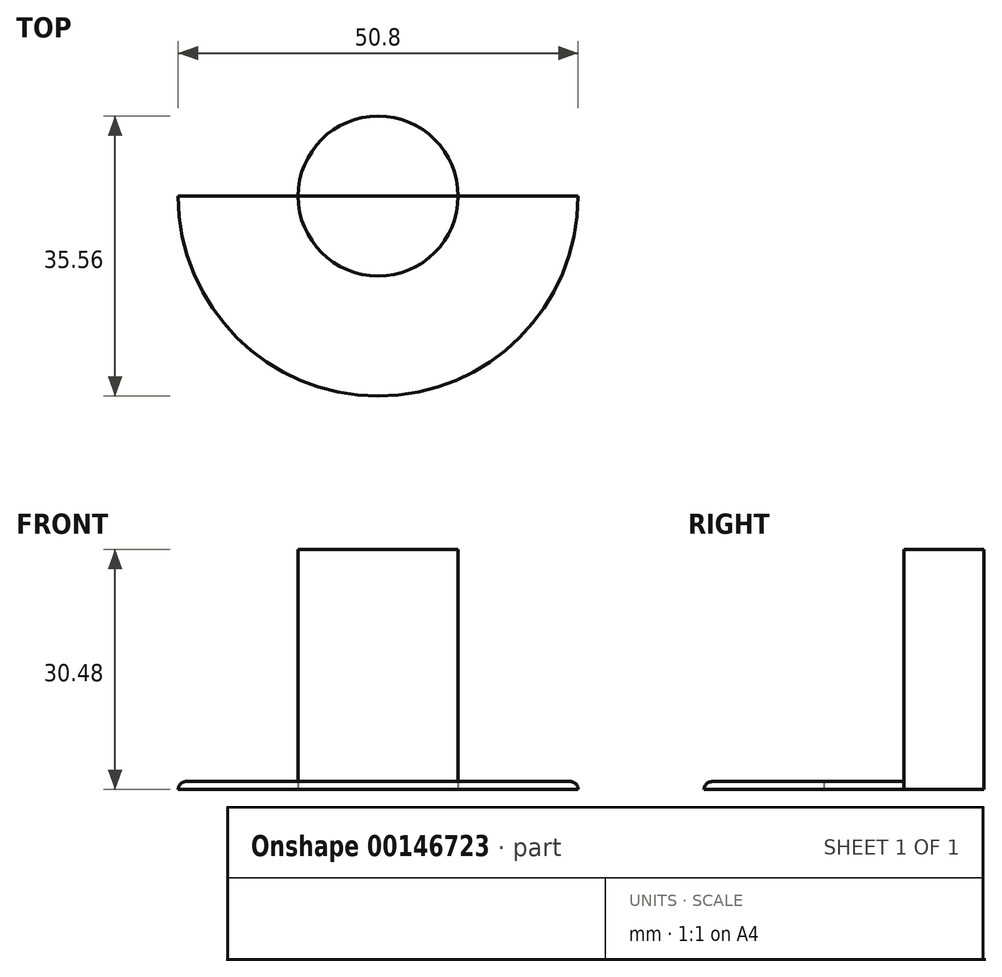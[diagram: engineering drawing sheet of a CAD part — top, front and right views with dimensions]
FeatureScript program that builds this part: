
annotation { "Feature Type Name" : "Feature", "Feature Type Description" : "" }
export const myFeature = defineFeature(function(context is Context, id is Id, definition is map)
    precondition{}
    {
        {
            assignVariable(context, id + "F0", {"name" : "R", "anyValue" : 2});
        }
        {
            var Q0;
            Q0=qCreatedBy(makeId("Top.planeOp"),FACE);
            var sketch = newSketch(context, id + "F1", { "sketchPlane" : qUnion([Q0])});
            skCircle(sketch, "E0", {"center": v(0, 0) * mm, "radius": 25.4 * mm});
            skCircle(sketch, "E1", {"center": v(0, 0) * mm, "radius": 10.16 * mm});
            skLineSegment(sketch, "E2", {"start": v(-25.4, 0) * mm, "end": v(25.4, 0) * mm});
            skSolve(sketch);
        }
        {
            var Q0;
            {var subQ0=sQuery(id+"F1.wireOp",EDGE,"E2");var subQ1=sQuery(id+"F1.wireOp",EDGE,"E0");var subQ2=makeQuery(id+"F1.imprint","INTERSECT",VERTEX,{"disambiguationData":[OD(0.0)],"derivedFrom":[subQ1,subQ0]});Q0=makeQuery(id+"F1.imprint","IMPRINT",FACE,{"disambiguationData":[TD([[makeQuery(id+"F1.imprint","IMPRINT",EDGE,{"disambiguationData":[TD([[subQ2,1.0]])],"derivedFrom":subQ1}),1.0]])]});}
            var Q1;
            {var subQ0=sQuery(id+"F1.wireOp",EDGE,"E2");var subQ1=sQuery(id+"F1.wireOp",EDGE,"E1");var subQ2=makeQuery(id+"F1.imprint","INTERSECT",VERTEX,{"disambiguationData":[OD(0.0)],"derivedFrom":[subQ1,subQ0]});Q1=makeQuery(id+"F1.imprint","IMPRINT",FACE,{"disambiguationData":[TD([[makeQuery(id+"F1.imprint","IMPRINT",EDGE,{"disambiguationData":[TD([[subQ2,1.0]])],"derivedFrom":subQ1}),1.0]])]});}
            extrude(context, id + "F2", {"entities" : qUnion([Q0, Q1]), "depth" : (getVariable(context, 'R') / 2) * mm});
        }
        {
            var Q0;
            Q0=makeQuery(id+"F2.opExtrude","CAP_EDGE",EDGE,{"disambiguationData":[OSD([sQuery(id+"F1.wireOp",EDGE,"E0")])],"isStart":false});
            fillet(context, id + "F3", {"entities" : qUnion([Q0]), "radius" : (getVariable(context, 'R') / 2) * mm, "tangentPropagation" : true, "allowEdgeOverflow" : false});
        }
        {
            var Q0;
            {var subQ0=sQuery(id+"F1.wireOp",EDGE,"E2");var subQ1=sQuery(id+"F1.wireOp",EDGE,"E1");var subQ2=makeQuery(id+"F1.imprint","INTERSECT",VERTEX,{"disambiguationData":[OD(0.0)],"derivedFrom":[subQ1,subQ0]});Q0=makeQuery(id+"F1.imprint","IMPRINT",FACE,{"disambiguationData":[TD([[makeQuery(id+"F1.imprint","IMPRINT",EDGE,{"disambiguationData":[TD([[subQ2,1.0]])],"derivedFrom":subQ1}),1.0]])]});}
            extrude(context, id + "F4", {"entities" : qUnion([Q0]), "operationType" : NewBodyOperationType.ADD, "depth" : 30.48 * mm});
        }
        {
            var Q0;
            Q0=makeQuery(id+"F2.opExtrude","CAP_FACE",FACE,{"disambiguationData":[OSD([sQuery(id+"F1.wireOp",EDGE,"E0"),sQuery(id+"F1.wireOp",EDGE,"E2")])],"isStart":true});
            var sketch = newSketch(context, id + "F5", { "sketchPlane" : qUnion([Q0])});
            skPoint(sketch, "E3", {"position": v(0, 0) * mm});
            skCircle(sketch, "E4", {"center": v(0, 0) * mm, "radius": 6.35 * mm});
            skLineSegment(sketch, "E5", {"start": v(0, 0) * mm, "end": v(-12.7, 0) * mm});
            skLineSegment(sketch, "E6", {"start": v(0, 0) * mm, "end": v(12.7, 0) * mm});
            skCircle(sketch, "E7", {"center": v(-12.7, 0) * mm, "radius": 2.54 * mm});
            skCircle(sketch, "E8", {"center": v(12.7, 0) * mm, "radius": 2.54 * mm});
            skCircle(sketch, "E9", {"center": v(0, 0) * mm, "radius": 3.18 * mm});
            skCircle(sketch, "E10", {"center": v(0, 0) * mm, "radius": 8.26 * mm});
            skSolve(sketch);
        }
        {
            var Q0;
            Q0=sQuery(id+"F5.wireOp",VERTEX,"E3");
            var Q1;
            Q1=makeQuery(id+"F2.opExtrude","SWEPT_BODY",BODY,{"disambiguationData":[OSD([sQuery(id+"F1.wireOp",EDGE,"E0")])]});
            hole(context, id + "F6", {"style" : HoleStyle.SIMPLE, "endStyle" : HoleEndStyle.THROUGH, "holeDiameter" : 16.5 * mm, "startFromSketch" : true, "locations" : qUnion([Q0]), "scope" : qUnion([Q1]), "isTappedThrough" : true});
        }
        {
            var Q0;
            {var subQ0=sQuery(id+"F5.wireOp",EDGE,"E5");var subQ1=sQuery(id+"F5.wireOp",EDGE,"E4");var subQ2=makeQuery(id+"F5.imprint","INTERSECT",VERTEX,{"derivedFrom":[subQ1,subQ0]});Q0=makeQuery(id+"F5.imprint","IMPRINT",FACE,{"disambiguationData":[TD([[makeQuery(id+"F5.imprint","IMPRINT",EDGE,{"disambiguationData":[TD([[subQ2,-1.0]])],"derivedFrom":subQ1}),1.0]])]});}
            var Q1;
            {var subQ0=sQuery(id+"F5.wireOp",EDGE,"E5");var subQ1=sQuery(id+"F5.wireOp",EDGE,"E4");var subQ2=makeQuery(id+"F5.imprint","INTERSECT",VERTEX,{"derivedFrom":[subQ1,subQ0]});Q1=makeQuery(id+"F5.imprint","IMPRINT",FACE,{"disambiguationData":[TD([[makeQuery(id+"F5.imprint","IMPRINT",EDGE,{"disambiguationData":[TD([[subQ2,-1.0]])],"derivedFrom":subQ1}),-1.0]])]});}
            extrude(context, id + "F7", {"entities" : qUnion([Q0, Q1]), "operationType" : NewBodyOperationType.ADD, "oppositeDirection" : true, "depth" : 12.7 * mm});
        }
        {
            var Q0;
            {var subQ0=sQuery(id+"F5.wireOp",EDGE,"E5");var subQ1=sQuery(id+"F5.wireOp",EDGE,"E4");var subQ2=makeQuery(id+"F5.imprint","INTERSECT",VERTEX,{"derivedFrom":[subQ1,subQ0]});Q0=makeQuery(id+"F5.imprint","IMPRINT",FACE,{"disambiguationData":[TD([[makeQuery(id+"F5.imprint","IMPRINT",EDGE,{"disambiguationData":[TD([[subQ2,-1.0]])],"derivedFrom":subQ1}),-1.0]])]});}
            extrude(context, id + "F8", {"entities" : qUnion([Q0]), "operationType" : NewBodyOperationType.ADD, "oppositeDirection" : true, "depth" : 30.48 * mm, "hasSecondDirection" : true, "secondDirectionOppositeDirection" : true, "secondDirectionDepth" : 27.94 * mm});
        }
        {
            var Q0;
            {var subQ0=sQuery(id+"F5.wireOp",EDGE,"E5");var subQ1=sQuery(id+"F1.wireOp",EDGE,"E2");Q0=makeQuery(id+"F8.boolean.opBoolean","MERGE",FACE,{"derivedFrom":[makeQuery(id+"F7.boolean.opBoolean","MERGE",FACE,{"derivedFrom":[makeQuery(id+"F6.hole-0.boolean.opBoolean","SPLIT",FACE,{"disambiguationData":[OD(0.0)],"derivedFrom":makeQuery(id+"F4.boolean.opBoolean","MERGE",FACE,{"derivedFrom":[makeQuery(id+"F2.opExtrude","SWEPT_FACE",FACE,{"disambiguationData":[OSD([subQ1])]}),makeQuery(id+"F4.opExtrude","SWEPT_FACE",FACE,{"disambiguationData":[OSD([subQ1])]})]})}),makeQuery(id+"F7.opExtrude","SWEPT_FACE",FACE,{"disambiguationData":[OSD([subQ0])]})]}),makeQuery(id+"F8.opExtrude","SWEPT_FACE",FACE,{"disambiguationData":[OSD([subQ0])]})]});}
            var sketch = newSketch(context, id + "F11", { "sketchPlane" : qUnion([Q0])});
            skLineSegment(sketch, "E11", {"start": v(-8.26, 12.7) * mm, "end": v(-8.26, 6.35) * mm});
            skLineSegment(sketch, "E12", {"start": v(-8.26, 6.35) * mm, "end": v(-8.26, 0) * mm});
            skLineSegment(sketch, "E13", {"start": v(-8.26, 6.35) * mm, "end": v(-14.6, 6.35) * mm});
            skLineSegment(sketch, "E14", {"start": v(-14.6, 6.35) * mm, "end": v(-8.26, 12.7) * mm});
            skCircle(sketch, "E15", {"center": v(-14.6, 6.35) * mm, "radius": 3 * mm});
            skSolve(sketch);
        }
        {
            var Q0;
            {var subQ0=sQuery(id+"F5.wireOp",EDGE,"E6");var subQ1=sQuery(id+"F1.wireOp",EDGE,"E2");Q0=makeQuery(id+"F8.boolean.opBoolean","MERGE",FACE,{"derivedFrom":[makeQuery(id+"F7.boolean.opBoolean","MERGE",FACE,{"derivedFrom":[makeQuery(id+"F6.hole-0.boolean.opBoolean","SPLIT",FACE,{"disambiguationData":[OD(1.0)],"derivedFrom":makeQuery(id+"F4.boolean.opBoolean","MERGE",FACE,{"derivedFrom":[makeQuery(id+"F2.opExtrude","SWEPT_FACE",FACE,{"disambiguationData":[OSD([subQ1])]}),makeQuery(id+"F4.opExtrude","SWEPT_FACE",FACE,{"disambiguationData":[OSD([subQ1])]})]})}),makeQuery(id+"F7.opExtrude","SWEPT_FACE",FACE,{"disambiguationData":[OSD([subQ0])]})]}),makeQuery(id+"F8.opExtrude","SWEPT_FACE",FACE,{"disambiguationData":[OSD([subQ0])]})]});}
            var sketch = newSketch(context, id + "F9", { "sketchPlane" : qUnion([Q0])});
            skLineSegment(sketch, "E16", {"start": v(8.26, 12.7) * mm, "end": v(8.26, 6.35) * mm});
            skLineSegment(sketch, "E17", {"start": v(8.26, 6.35) * mm, "end": v(8.26, 0) * mm});
            skLineSegment(sketch, "E18", {"start": v(8.26, 0) * mm, "end": v(8.26, 0) * mm});
            skLineSegment(sketch, "E19", {"start": v(8.26, 6.35) * mm, "end": v(14.6, 6.35) * mm});
            skLineSegment(sketch, "E20", {"start": v(8.26, 12.7) * mm, "end": v(14.6, 6.35) * mm});
            skCircle(sketch, "E21", {"center": v(14.6, 6.35) * mm, "radius": 3 * mm});
            skSolve(sketch);
        }
        {
            var Q0;
            {var subQ0=sQuery(id+"F11.wireOp",EDGE,"E14");var subQ1=sQuery(id+"F11.wireOp",EDGE,"E13");var subQ2=makeQuery(id+"F11.imprint","INTERSECT",VERTEX,{"derivedFrom":[subQ1,subQ0]});Q0=makeQuery(id+"F11.imprint","IMPRINT",FACE,{"disambiguationData":[TD([[makeQuery(id+"F11.imprint","IMPRINT",EDGE,{"disambiguationData":[TD([[subQ2,1.0]])],"derivedFrom":subQ1}),1.0]])]});}
            var Q1;
            {var subQ0=sQuery(id+"F11.wireOp",EDGE,"E14");var subQ1=sQuery(id+"F11.wireOp",EDGE,"E13");var subQ2=makeQuery(id+"F11.imprint","INTERSECT",VERTEX,{"derivedFrom":[subQ1,subQ0]});Q1=makeQuery(id+"F11.imprint","IMPRINT",FACE,{"disambiguationData":[TD([[makeQuery(id+"F11.imprint","IMPRINT",EDGE,{"disambiguationData":[TD([[subQ2,1.0]])],"derivedFrom":subQ1}),-1.0]])]});}
            var Q2;
            {var subQ0=sQuery(id+"F9.wireOp",EDGE,"E20");var subQ1=sQuery(id+"F9.wireOp",EDGE,"E19");var subQ2=makeQuery(id+"F9.imprint","INTERSECT",VERTEX,{"derivedFrom":[subQ1,subQ0]});Q2=makeQuery(id+"F9.imprint","IMPRINT",FACE,{"disambiguationData":[TD([[makeQuery(id+"F9.imprint","IMPRINT",EDGE,{"disambiguationData":[TD([[subQ2,1.0]])],"derivedFrom":subQ1}),1.0]])]});}
            var Q3;
            {var subQ0=sQuery(id+"F9.wireOp",EDGE,"E20");var subQ1=sQuery(id+"F9.wireOp",EDGE,"E19");var subQ2=makeQuery(id+"F9.imprint","INTERSECT",VERTEX,{"derivedFrom":[subQ1,subQ0]});Q3=makeQuery(id+"F9.imprint","IMPRINT",FACE,{"disambiguationData":[TD([[makeQuery(id+"F9.imprint","IMPRINT",EDGE,{"disambiguationData":[TD([[subQ2,1.0]])],"derivedFrom":subQ1}),-1.0]])]});}
            extrude(context, id + "F10", {"entities" : qUnion([Q0, Q1, Q2, Q3]), "operationType" : NewBodyOperationType.REMOVE, "oppositeDirection" : true, "depth" : 7 * mm});
        }
    });
